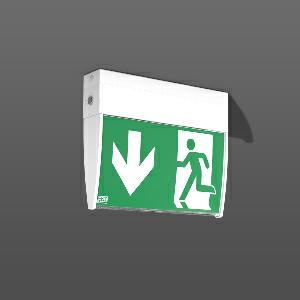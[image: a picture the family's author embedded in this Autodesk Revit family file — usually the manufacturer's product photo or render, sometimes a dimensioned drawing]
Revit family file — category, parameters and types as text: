
# Revit family: gsun_d_671996_002_2_bbd5
name_source: partatom
category: Lighting Fixtures
units: mm (PartAtom-declared; Revit-internal decimal feet)

## family parameters
Cut with Voids When Loaded = No
Host = Face
Light Source = No
Part Type = Normal
Room Calculation Point = No
Round Connector Dimension = Use Diameter
Shared = No

## types (1)
- GSUN D
    Apparent Load = 0 VA
    Default Elevation = 1800 mm
    Description = Series: GSUN D
Luminaire for escape route identification. Housing: extruded aluminium profile, powder-coated. 4 legends and 1 white lay in plastic sheet included. Universal mounting kit for ceiling and wall surface mounting. Driver integrated. Suitable for connection to central battery systems. 
Colour: white
Length: 247 mm
Width: 45 mm
Height: 200 mm
Weight: 1 kg
Operating mode: maintained power mode
Viewing Distance: 24 m
Lamp: LED
Socket: without socket
Colour temperature: 4000K
System power: 3.7 W
System power, emergency: 3.7 W
Control gear: Converter not necessary
Protection class: I
Type of protection: IP 30
    Height = 200 mm  [stored 0.656168 ft]
    Lamp = 0 x
    Length = 247 mm
    Luminous efficacy = 0 lm/W
    Manufacturer = RZB
    ModVariant = No
    Model = 671996.002.2
    Mounting Place = Ceiling, Wall
    Mounting Type = Surface mounted
    Number of Poles = 1
    OnlyDefault = Yes
    Power Factor = 1
    Product Name = GSUN D
    Product group = Surface mounted ceiling and wall luminaires
    ProductGroupID = 305
    Protection Class = Protection class I
    Protection Degree = IP 30
    RLX_Detail_Level = 1
    RLX_Emergency_Light_Flux = 0 lm
    RLX_Emergency_Type = 0
    RLX_Emergency_Type_DB = No
    RlxData = <blob elided: 30001 chars, md5=1d3940bc>
    Standby Power = 0 W
    System Light Flux = 0 lm
    System Power = 0 W
    Type Comments = Product without accessories
    Type Image = 671995.002.1.jpg
    URL = http://relux.com
    VarID = ---
    Voltage = 230 V
    Voltage Range = 220-240 V
    Weight = 0.00 kg
    Width = 45 mm

note: [stored X ft] marks values corroborated as IEEE doubles in the binary element streams (Revit-internal decimal feet)

## geometry (parser evidence)
native form markers: Blend x4, Sweep x10
no freeform markers — native parametric forms only
